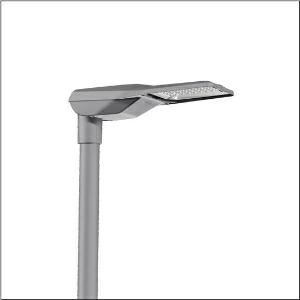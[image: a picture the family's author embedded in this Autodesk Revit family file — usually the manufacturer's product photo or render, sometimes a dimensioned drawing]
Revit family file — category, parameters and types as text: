
# Revit family: streetlight_sl_21_iq_mini___st0_5a_5xe2b31d08gb_9f53
name_source: partatom
category: Lighting Fixtures
units: mm (PartAtom-declared; Revit-internal decimal feet)

## family parameters
Cut with Voids When Loaded = No
Host = Face
Light Source = No
Part Type = Normal
Room Calculation Point = No
Round Connector Dimension = Use Diameter
Shared = No

## types (1)
- --- (1 x LED, 5680 lm, 37.1 W, 3000K)
    Apparent Load = 37 VA
    CIE Flux Codes = 41 75 97 100 100
    Color Rendering = 70
    Color Temperature = 3000K
    Default Elevation = 1800 mm
    Description = Streetlight SL 21 iQ mini, mast luminaire, primary light control with lens, of PMMA, primary optical cover: cover, of toughened safety glass, transparent, light distribution: ST0.5a, light emission: direct distribution, primary light characteristic: asymmetric, installation type: post-top, side-entry, LED, High Power LED, rated luminous flux: 5.680lm, luminous efficacy: 153lm/W, light colour: 730, colour temperature: 3000K, control: Auto-Match, Temp-Guard, Lumen-Switch, Night-Set, Smart-Wire, Light-Fading, Desk-Remote (wireless, voltage-free reading and setting of iQ features in the workshop via application-optimized NFC function/RFID function), optimised constant luminous flux control (CLO 2.0), presetting dimming linear, mains connection: 220..240V, AC, 50/60Hz, start of lifetime: 37W, end of service life: 39W, reduction: 18W, luminaire housing, of diecast aluminium, powder-coated, Siteco® metallic grey (DB 702S), corrosivity category C5 mid according to DIN EN ISO 12944, please order mast flange separately, inclination adjustable: 0°, 5°, 10°, 15°, sealing non-destructively replaceable, multi-level sealing system, length: 628mm, width: 235mm, height: 110mm, mast flange for spigot size: 42mm (side-entry): 5XC10008XM4, 60/48mm (side-entry/post-top): 5XC10108XM2, 76/60mm (side-entry/post-top): 5XC10108XM1, protection rating (complete): IP66, insulation class (complete): insulation class II (safety insulation), certification: CE, ENEC, ENEC+, VDE, impact resistance: IK09, permissible operating ambient temperature for outdoor applications: -40..+50°C, standard-compliant lighting for roads and squares, packaging unit: 1 piece

Light Distribution: ST0.5a
    Height = 110 mm
    Lamp = 1 x LED
    Lamp Light Flux = 5680 lm
    Lamp Power = 37.1 W
    Lamp count = 1
    Length = 625 mm
    Luminous efficacy = 153 lm/W
    Manufacturer = Siteco
    ModVariant = No
    Model = 5XE2B31D08GB
    Number of Poles = 1
    OnlyDefault = Yes
    Power Factor = 1
    Product Name = Streetlight SL 21 iQ mini | ST0.5a
    Product group = mast luminaire | pylon top
    ProductGroupID = 6100
    Protection Class = Protection class II
    Protection Degree = IP 66
    RLX_Detail_Level = 1
    RLX_Emergency_Light_Flux = 0 lm
    RLX_Emergency_Type = 0
    RLX_Emergency_Type_DB = No
    RlxData = <blob elided: 103321 chars, md5=bf0e6ec9>
    Socket = socket
    Standby Power = 0 W
    System Light Flux = 5680 lm
    System Power = 37 W
    Type Comments = factory setting: luminous flux: 100 % | dim-lin: 254 | 385 mA
    Type Image = l_1003519.jpg
    URL = http://relux.com
    VarID = @adj_143889
    Voltage = 0 V
    Weight = 0.00 kg
    Width = 234 mm

## geometry (parser evidence)
native form markers: Blend x4, Sweep x8
no freeform markers — native parametric forms only
